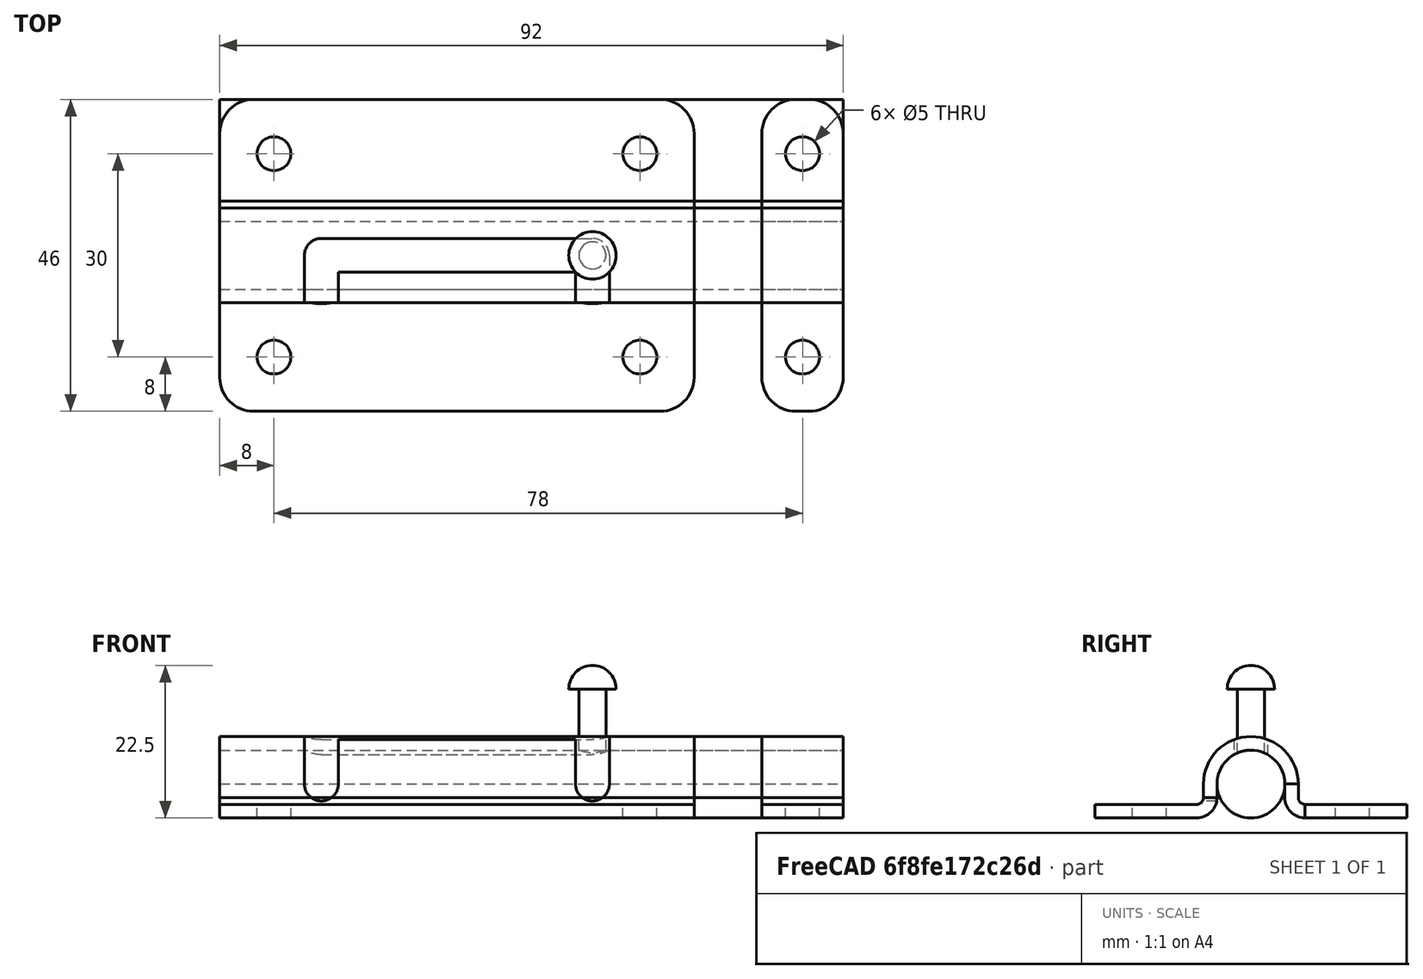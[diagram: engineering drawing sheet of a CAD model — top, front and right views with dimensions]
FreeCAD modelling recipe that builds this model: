
FCSTD DOCUMENT  (FreeCAD 0.18R13524 (Git))
Label: TRINCO
License: All rights reserved
LicenseURL: http://en.wikipedia.org/wiki/All_rights_reserved
objects: Part::Cut×14, Part::Cylinder×12, Part::Box×5, Part::FeaturePython×3, Part::MultiFuse×2, Part::Sphere×1, Part::Fillet×1
note: 38 computed .brp shape members not serialized (recipe doc carries the construction recipe); baked Part::Feature solids carry a one-line shape summary decoded from their .brp

FEATURE [Part::Box] Box  label="Cube"
  AttacherType = Attacher::AttachEngine3D
  Height = 2
  Length = 92
  Placement = pos=(0,8,0) rot=(0,0,1;0rad)
  Width = 15
FEATURE [Part::FeaturePython] Bend  # WARN: FeaturePython — macro-defined, semantics opaque (R4)
  angle = 90
  baseObject = -> Box [Face3]
  gap1 = 0
  gap2 = 0
  invert = false
  length = 2
  miterangle1 = 0
  miterangle2 = 0
  radius = 1
  reliefd = 1
  reliefw = 0.5
FEATURE [Part::FeaturePython] Bend001  # WARN: FeaturePython — macro-defined, semantics opaque (R4)
  angle = 180
  baseObject = -> Bend [Face1]
  gap1 = 0
  gap2 = 0
  invert = true
  length = 2
  miterangle1 = 0
  miterangle2 = 0
  radius = 5
  reliefd = 1
  reliefw = 0.5
FEATURE [Part::FeaturePython] Bend002  # WARN: FeaturePython — macro-defined, semantics opaque (R4)
  angle = 90
  baseObject = -> Bend001 [Face1]
  gap1 = 0
  gap2 = 0
  invert = false
  length = 15
  miterangle1 = 0
  miterangle2 = 0
  radius = 1
  reliefd = 1
  reliefw = 0.5
FEATURE [Part::Box] Box001  label="Cube001"
  AttacherType = Attacher::AttachEngine3D
  Height = 12
  Length = 10
  Placement = pos=(70,-30,0) rot=(0,0,1;0rad)
  Width = 60
FEATURE [Part::Cut] Cut
  Base = -> Bend002
  Tool = -> Box001
FEATURE [Part::Cylinder] Cylinder
  Angle = 360
  AttacherType = Attacher::AttachEngine3D
  Height = 92
  Placement = pos=(0,0,5) rot=(0,1,0;1.5708rad)
  Radius = 5
FEATURE [Part::Cylinder] Cylinder001
  Angle = 360
  AttacherType = Attacher::AttachEngine3D
  Height = 10
  Placement = pos=(55,0,9) rot=(0,0,1;0rad)
  Radius = 2
FEATURE [Part::Sphere] Sphere
  Angle1 = -90
  Angle2 = 90
  Angle3 = 180
  AttacherType = Attacher::AttachEngine3D
  Placement = pos=(55,0,19) rot=(1,0,0;1.5708rad)
  Radius = 3.5
FEATURE [Part::Cylinder] Cylinder002
  Angle = 360
  AttacherType = Attacher::AttachEngine3D
  Height = 20
  Placement = pos=(15,0,0) rot=(0,0,1;0rad)
  Radius = 2.5
FEATURE [Part::Cylinder] Cylinder003
  Angle = 360
  AttacherType = Attacher::AttachEngine3D
  Height = 20
  Placement = pos=(55,0,0) rot=(0,0,1;0rad)
  Radius = 2.5
FEATURE [Part::Box] Box002  label="Cube002"
  AttacherType = Attacher::AttachEngine3D
  Height = 15
  Length = 40
  Placement = pos=(15,-2.5,0) rot=(0,0,1;0rad)
  Width = 5
FEATURE [Part::Cylinder] Cylinder004
  Angle = 360
  AttacherType = Attacher::AttachEngine3D
  Height = 20
  Placement = pos=(15,-3,5) rot=(1,0,0;1.5708rad)
  Radius = 2.5
FEATURE [Part::Cylinder] Cylinder005
  Angle = 360
  AttacherType = Attacher::AttachEngine3D
  Height = 20
  Placement = pos=(55,-3,5) rot=(1,0,0;1.5708rad)
  Radius = 2.5
FEATURE [Part::Box] Box003  label="Cube003"
  AttacherType = Attacher::AttachEngine3D
  Height = 15
  Length = 5
  Placement = pos=(52.5,-8,5) rot=(0,0,1;0rad)
  Width = 8
FEATURE [Part::Box] Box004  label="Cube004"
  AttacherType = Attacher::AttachEngine3D
  Height = 15
  Length = 5
  Placement = pos=(12.5,-8,5) rot=(0,0,1;0rad)
  Width = 8
FEATURE [Part::Cylinder] Cylinder006
  Angle = 360
  AttacherType = Attacher::AttachEngine3D
  Height = 10
  Placement = pos=(8,15,0) rot=(0,0,1;0rad)
  Radius = 2.5
FEATURE [Part::Cylinder] Cylinder007
  Angle = 360
  AttacherType = Attacher::AttachEngine3D
  Height = 10
  Placement = pos=(62,15,0) rot=(0,0,1;0rad)
  Radius = 2.5
FEATURE [Part::Cylinder] Cylinder008
  Angle = 360
  AttacherType = Attacher::AttachEngine3D
  Height = 10
  Placement = pos=(86,15,0) rot=(0,0,1;0rad)
  Radius = 2.5
FEATURE [Part::Cylinder] Cylinder009
  Angle = 360
  AttacherType = Attacher::AttachEngine3D
  Height = 10
  Placement = pos=(86,-15,0) rot=(0,0,1;0rad)
  Radius = 2.5
FEATURE [Part::Cylinder] Cylinder010
  Angle = 360
  AttacherType = Attacher::AttachEngine3D
  Height = 10
  Placement = pos=(62,-15,0) rot=(0,0,1;0rad)
  Radius = 2.5
FEATURE [Part::Cylinder] Cylinder011
  Angle = 360
  AttacherType = Attacher::AttachEngine3D
  Height = 10
  Placement = pos=(8,-15,0) rot=(0,0,1;0rad)
  Radius = 2.5
FEATURE [Part::Cut] Cut001
  Base = -> Cut
  Tool = -> Cylinder002
FEATURE [Part::Cut] Cut002
  Base = -> Cut001
  Tool = -> Cylinder003
FEATURE [Part::Cut] Cut003
  Base = -> Cut002
  Tool = -> Box002
FEATURE [Part::Cut] Cut004
  Base = -> Cut003
  Tool = -> Cylinder004
FEATURE [Part::Cut] Cut005
  Base = -> Cut004
  Tool = -> Cylinder005
FEATURE [Part::Cut] Cut006
  Base = -> Cut005
  Tool = -> Box003
FEATURE [Part::Cut] Cut007
  Base = -> Cut006
  Tool = -> Box004
FEATURE [Part::Cut] Cut008
  Base = -> Cut007
  Tool = -> Cylinder006
FEATURE [Part::Cut] Cut009
  Base = -> Cut008
  Tool = -> Cylinder007
FEATURE [Part::Cut] Cut010
  Base = -> Cut009
  Tool = -> Cylinder008
FEATURE [Part::Cut] Cut011
  Base = -> Cut010
  Tool = -> Cylinder009
FEATURE [Part::Cut] Cut012
  Base = -> Cut011
  Tool = -> Cylinder010
FEATURE [Part::Cut] Cut013
  Base = -> Cut012
  Tool = -> Cylinder011
FEATURE [Part::MultiFuse] Fusion
  Shapes = -> [Cylinder,Cylinder001]
FEATURE [Part::MultiFuse] Fusion001
  Shapes = -> [Fusion,Sphere]
FEATURE [Part::Fillet] Fillet
  Base = -> Cut013
  Edges = 8 edges r=5: [Edge2,Edge4,Edge14,Edge56,Edge115,Edge117,Edge131,Edge158]
